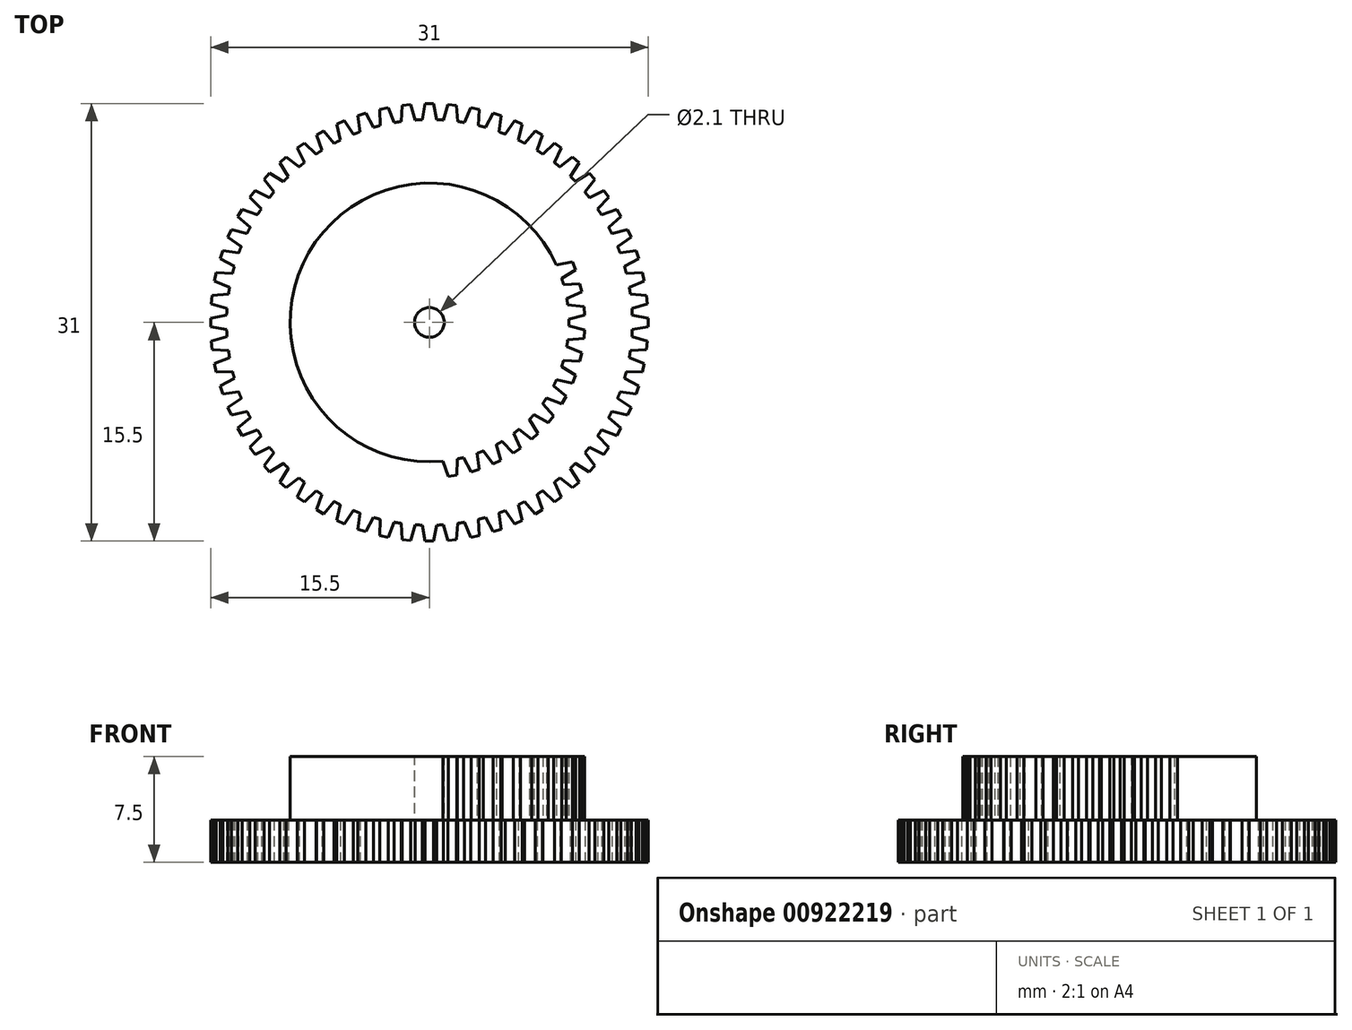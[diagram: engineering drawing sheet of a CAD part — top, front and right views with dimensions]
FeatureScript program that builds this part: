
annotation { "Feature Type Name" : "Feature", "Feature Type Description" : "" }
export const myFeature = defineFeature(function(context is Context, id is Id, definition is map)
    precondition{}
    {
        {
            var Q0;
            Q0=qCreatedBy(makeId("Top.planeOp"),FACE);
            var sketch = newSketch(context, id + "F0", { "sketchPlane" : qUnion([Q0])});
            skCircle(sketch, "E0", {"center": v(0, 0) * mm, "radius": 15 * mm, "construction": true});
            skCircle(sketch, "E1", {"center": v(0, 0) * mm, "radius": 15.5 * mm, "construction": true});
            skCircle(sketch, "E2", {"center": v(0, 0) * mm, "radius": 14.38 * mm});
            skLineSegment(sketch, "E3", {"start": v(0, 14.38) * mm, "end": v(0.5, 14.38) * mm, "construction": true});
            skLineSegment(sketch, "E4", {"start": v(0, 14.38) * mm, "end": v(-0.5, 14.38) * mm, "construction": true});
            skLineSegment(sketch, "E5", {"start": v(-1.79, 7.07) * mm, "end": v(-0.5, 14.37) * mm, "construction": true});
            skLineSegment(sketch, "E6", {"start": v(1.79, 7.07) * mm, "end": v(0.3, 15.5) * mm, "construction": true});
            skLineSegment(sketch, "E7", {"start": v(-1.79, 7.08) * mm, "end": v(-0.3, 15.5) * mm});
            skLineSegment(sketch, "E8", {"start": v(0.3, 15.5) * mm, "end": v(-0.3, 15.5) * mm});
            skLineSegment(sketch, "E9", {"start": v(0.3, 15.5) * mm, "end": v(0.5, 14.37) * mm});
            skLineSegment(sketch, "E10.1.0", {"start": v(-2.52, 6.85) * mm, "end": v(-1.92, 15.38) * mm});
            skLineSegment(sketch, "E10.1.1", {"start": v(-1.32, 15.44) * mm, "end": v(-1.92, 15.38) * mm});
            skLineSegment(sketch, "E10.1.2", {"start": v(-1.32, 15.44) * mm, "end": v(-1, 14.34) * mm});
            skLineSegment(sketch, "E10.2.0", {"start": v(-3.22, 6.55) * mm, "end": v(-3.52, 15.1) * mm});
            skLineSegment(sketch, "E10.2.1", {"start": v(-2.93, 15.22) * mm, "end": v(-3.52, 15.1) * mm});
            skLineSegment(sketch, "E10.2.2", {"start": v(-2.93, 15.22) * mm, "end": v(-2.5, 14.16) * mm});
            skLineSegment(sketch, "E11.1.3.0", {"start": v(-3.89, 6.18) * mm, "end": v(-5.08, 14.65) * mm});
            skLineSegment(sketch, "E11.3.3.0", {"start": v(-4.5, 14.83) * mm, "end": v(-5.08, 14.65) * mm});
            skLineSegment(sketch, "E11.6.3.0", {"start": v(-4.5, 14.83) * mm, "end": v(-3.96, 13.82) * mm});
            skLineSegment(sketch, "E11.1.4.0", {"start": v(-4.51, 5.74) * mm, "end": v(-6.58, 14.03) * mm});
            skLineSegment(sketch, "E11.3.4.0", {"start": v(-6.03, 14.28) * mm, "end": v(-6.58, 14.03) * mm});
            skLineSegment(sketch, "E11.6.4.0", {"start": v(-6.03, 14.28) * mm, "end": v(-5.39, 13.33) * mm});
            skLineSegment(sketch, "E11.1.5.0", {"start": v(-5.09, 5.24) * mm, "end": v(-8.01, 13.27) * mm});
            skLineSegment(sketch, "E11.3.5.0", {"start": v(-7.49, 13.57) * mm, "end": v(-8.01, 13.27) * mm});
            skLineSegment(sketch, "E11.6.5.0", {"start": v(-7.49, 13.57) * mm, "end": v(-6.75, 12.7) * mm});
            skLineSegment(sketch, "E11.1.6.0", {"start": v(-5.6, 4.68) * mm, "end": v(-9.35, 12.36) * mm});
            skLineSegment(sketch, "E11.3.6.0", {"start": v(-8.86, 12.71) * mm, "end": v(-9.35, 12.36) * mm});
            skLineSegment(sketch, "E11.6.6.0", {"start": v(-8.86, 12.71) * mm, "end": v(-8.04, 11.92) * mm});
            skLineSegment(sketch, "E11.1.7.0", {"start": v(-6.06, 4.07) * mm, "end": v(-10.6, 11.31) * mm});
            skLineSegment(sketch, "E11.3.7.0", {"start": v(-10.15, 11.72) * mm, "end": v(-10.6, 11.31) * mm});
            skLineSegment(sketch, "E11.6.7.0", {"start": v(-10.15, 11.72) * mm, "end": v(-9.24, 11.01) * mm});
            skLineSegment(sketch, "E11.1.8.0", {"start": v(-6.46, 3.4) * mm, "end": v(-11.72, 10.15) * mm});
            skLineSegment(sketch, "E11.3.8.0", {"start": v(-11.31, 10.6) * mm, "end": v(-11.72, 10.15) * mm});
            skLineSegment(sketch, "E11.6.8.0", {"start": v(-11.31, 10.6) * mm, "end": v(-10.34, 9.99) * mm});
            skLineSegment(sketch, "E11.1.9.0", {"start": v(-6.78, 2.72) * mm, "end": v(-12.71, 8.86) * mm});
            skLineSegment(sketch, "E11.3.9.0", {"start": v(-12.36, 9.35) * mm, "end": v(-12.71, 8.86) * mm});
            skLineSegment(sketch, "E11.6.9.0", {"start": v(-12.36, 9.35) * mm, "end": v(-11.33, 8.85) * mm});
            skLineSegment(sketch, "E11.1.10.0", {"start": v(-7.02, 2) * mm, "end": v(-13.57, 7.49) * mm});
            skLineSegment(sketch, "E11.3.10.0", {"start": v(-13.27, 8.01) * mm, "end": v(-13.57, 7.49) * mm});
            skLineSegment(sketch, "E11.6.10.0", {"start": v(-13.27, 8.01) * mm, "end": v(-12.2, 7.62) * mm});
            skLineSegment(sketch, "E11.1.11.0", {"start": v(-7.2, 1.25) * mm, "end": v(-14.28, 6.03) * mm});
            skLineSegment(sketch, "E11.3.11.0", {"start": v(-14.03, 6.58) * mm, "end": v(-14.28, 6.03) * mm});
            skLineSegment(sketch, "E11.6.11.0", {"start": v(-14.03, 6.58) * mm, "end": v(-12.92, 6.3) * mm});
            skLineSegment(sketch, "E11.1.12.0", {"start": v(-7.28, 0.49) * mm, "end": v(-14.83, 4.5) * mm});
            skLineSegment(sketch, "E11.3.12.0", {"start": v(-14.65, 5.08) * mm, "end": v(-14.83, 4.5) * mm});
            skLineSegment(sketch, "E11.6.12.0", {"start": v(-14.65, 5.08) * mm, "end": v(-13.5, 4.92) * mm});
            skLineSegment(sketch, "E11.1.13.0", {"start": v(-7.3, -0.28) * mm, "end": v(-15.22, 2.93) * mm});
            skLineSegment(sketch, "E11.3.13.0", {"start": v(-15.1, 3.52) * mm, "end": v(-15.22, 2.93) * mm});
            skLineSegment(sketch, "E11.6.13.0", {"start": v(-15.1, 3.52) * mm, "end": v(-13.95, 3.48) * mm});
            skLineSegment(sketch, "E11.1.14.0", {"start": v(-7.23, -1.04) * mm, "end": v(-15.44, 1.32) * mm});
            skLineSegment(sketch, "E11.3.14.0", {"start": v(-15.38, 1.92) * mm, "end": v(-15.44, 1.32) * mm});
            skLineSegment(sketch, "E11.6.14.0", {"start": v(-15.38, 1.92) * mm, "end": v(-14.24, 2) * mm});
            skLineSegment(sketch, "E11.1.15.0", {"start": v(-7.08, -1.79) * mm, "end": v(-15.5, -0.3) * mm});
            skLineSegment(sketch, "E11.3.15.0", {"start": v(-15.5, 0.3) * mm, "end": v(-15.5, -0.3) * mm});
            skLineSegment(sketch, "E11.6.15.0", {"start": v(-15.5, 0.3) * mm, "end": v(-14.37, 0.5) * mm});
            skLineSegment(sketch, "E11.1.16.0", {"start": v(-6.85, -2.52) * mm, "end": v(-15.38, -1.92) * mm});
            skLineSegment(sketch, "E11.3.16.0", {"start": v(-15.44, -1.32) * mm, "end": v(-15.38, -1.92) * mm});
            skLineSegment(sketch, "E11.6.16.0", {"start": v(-15.44, -1.32) * mm, "end": v(-14.34, -1) * mm});
            skLineSegment(sketch, "E11.1.17.0", {"start": v(-6.55, -3.22) * mm, "end": v(-15.1, -3.52) * mm});
            skLineSegment(sketch, "E11.3.17.0", {"start": v(-15.22, -2.93) * mm, "end": v(-15.1, -3.52) * mm});
            skLineSegment(sketch, "E11.6.17.0", {"start": v(-15.22, -2.93) * mm, "end": v(-14.16, -2.5) * mm});
            skLineSegment(sketch, "E11.1.18.0", {"start": v(-6.18, -3.89) * mm, "end": v(-14.65, -5.08) * mm});
            skLineSegment(sketch, "E11.3.18.0", {"start": v(-14.83, -4.5) * mm, "end": v(-14.65, -5.08) * mm});
            skLineSegment(sketch, "E11.6.18.0", {"start": v(-14.83, -4.5) * mm, "end": v(-13.82, -3.96) * mm});
            skLineSegment(sketch, "E11.1.19.0", {"start": v(-5.74, -4.51) * mm, "end": v(-14.03, -6.58) * mm});
            skLineSegment(sketch, "E11.3.19.0", {"start": v(-14.28, -6.03) * mm, "end": v(-14.03, -6.58) * mm});
            skLineSegment(sketch, "E11.6.19.0", {"start": v(-14.28, -6.03) * mm, "end": v(-13.33, -5.39) * mm});
            skLineSegment(sketch, "E11.1.20.0", {"start": v(-5.24, -5.09) * mm, "end": v(-13.27, -8.01) * mm});
            skLineSegment(sketch, "E11.3.20.0", {"start": v(-13.57, -7.49) * mm, "end": v(-13.27, -8.01) * mm});
            skLineSegment(sketch, "E11.6.20.0", {"start": v(-13.57, -7.49) * mm, "end": v(-12.7, -6.75) * mm});
            skLineSegment(sketch, "E11.1.21.0", {"start": v(-4.68, -5.6) * mm, "end": v(-12.36, -9.35) * mm});
            skLineSegment(sketch, "E11.3.21.0", {"start": v(-12.71, -8.86) * mm, "end": v(-12.36, -9.35) * mm});
            skLineSegment(sketch, "E11.6.21.0", {"start": v(-12.71, -8.86) * mm, "end": v(-11.92, -8.04) * mm});
            skLineSegment(sketch, "E11.1.22.0", {"start": v(-4.07, -6.06) * mm, "end": v(-11.31, -10.6) * mm});
            skLineSegment(sketch, "E11.3.22.0", {"start": v(-11.72, -10.15) * mm, "end": v(-11.31, -10.6) * mm});
            skLineSegment(sketch, "E11.6.22.0", {"start": v(-11.72, -10.15) * mm, "end": v(-11.01, -9.24) * mm});
            skLineSegment(sketch, "E11.1.23.0", {"start": v(-3.4, -6.46) * mm, "end": v(-10.15, -11.72) * mm});
            skLineSegment(sketch, "E11.3.23.0", {"start": v(-10.6, -11.31) * mm, "end": v(-10.15, -11.72) * mm});
            skLineSegment(sketch, "E11.6.23.0", {"start": v(-10.6, -11.31) * mm, "end": v(-9.99, -10.34) * mm});
            skLineSegment(sketch, "E11.1.24.0", {"start": v(-2.72, -6.78) * mm, "end": v(-8.86, -12.71) * mm});
            skLineSegment(sketch, "E11.3.24.0", {"start": v(-9.35, -12.36) * mm, "end": v(-8.86, -12.71) * mm});
            skLineSegment(sketch, "E11.6.24.0", {"start": v(-9.35, -12.36) * mm, "end": v(-8.85, -11.33) * mm});
            skLineSegment(sketch, "E11.1.25.0", {"start": v(-2, -7.02) * mm, "end": v(-7.49, -13.57) * mm});
            skLineSegment(sketch, "E11.3.25.0", {"start": v(-8.01, -13.27) * mm, "end": v(-7.49, -13.57) * mm});
            skLineSegment(sketch, "E11.6.25.0", {"start": v(-8.01, -13.27) * mm, "end": v(-7.62, -12.2) * mm});
            skLineSegment(sketch, "E11.1.26.0", {"start": v(-1.25, -7.2) * mm, "end": v(-6.03, -14.28) * mm});
            skLineSegment(sketch, "E11.3.26.0", {"start": v(-6.58, -14.03) * mm, "end": v(-6.03, -14.28) * mm});
            skLineSegment(sketch, "E11.6.26.0", {"start": v(-6.58, -14.03) * mm, "end": v(-6.3, -12.92) * mm});
            skLineSegment(sketch, "E11.1.27.0", {"start": v(-0.49, -7.28) * mm, "end": v(-4.5, -14.83) * mm});
            skLineSegment(sketch, "E11.3.27.0", {"start": v(-5.08, -14.65) * mm, "end": v(-4.5, -14.83) * mm});
            skLineSegment(sketch, "E11.6.27.0", {"start": v(-5.08, -14.65) * mm, "end": v(-4.92, -13.5) * mm});
            skLineSegment(sketch, "E11.1.28.0", {"start": v(0.28, -7.3) * mm, "end": v(-2.93, -15.22) * mm});
            skLineSegment(sketch, "E11.3.28.0", {"start": v(-3.52, -15.1) * mm, "end": v(-2.93, -15.22) * mm});
            skLineSegment(sketch, "E11.6.28.0", {"start": v(-3.52, -15.1) * mm, "end": v(-3.48, -13.95) * mm});
            skLineSegment(sketch, "E11.1.29.0", {"start": v(1.04, -7.23) * mm, "end": v(-1.32, -15.44) * mm});
            skLineSegment(sketch, "E11.3.29.0", {"start": v(-1.92, -15.38) * mm, "end": v(-1.32, -15.44) * mm});
            skLineSegment(sketch, "E11.6.29.0", {"start": v(-1.92, -15.38) * mm, "end": v(-2, -14.24) * mm});
            skLineSegment(sketch, "E12.1.30.0", {"start": v(1.79, -7.08) * mm, "end": v(0.3, -15.5) * mm});
            skLineSegment(sketch, "E12.3.30.0", {"start": v(-0.3, -15.5) * mm, "end": v(0.3, -15.5) * mm});
            skLineSegment(sketch, "E12.6.30.0", {"start": v(-0.3, -15.5) * mm, "end": v(-0.5, -14.37) * mm});
            skLineSegment(sketch, "E12.1.31.0", {"start": v(2.52, -6.85) * mm, "end": v(1.92, -15.38) * mm});
            skLineSegment(sketch, "E12.3.31.0", {"start": v(1.32, -15.44) * mm, "end": v(1.92, -15.38) * mm});
            skLineSegment(sketch, "E12.6.31.0", {"start": v(1.32, -15.44) * mm, "end": v(1, -14.34) * mm});
            skLineSegment(sketch, "E12.1.32.0", {"start": v(3.22, -6.55) * mm, "end": v(3.52, -15.1) * mm});
            skLineSegment(sketch, "E12.3.32.0", {"start": v(2.93, -15.22) * mm, "end": v(3.52, -15.1) * mm});
            skLineSegment(sketch, "E12.6.32.0", {"start": v(2.93, -15.22) * mm, "end": v(2.5, -14.16) * mm});
            skLineSegment(sketch, "E12.1.33.0", {"start": v(3.89, -6.18) * mm, "end": v(5.08, -14.65) * mm});
            skLineSegment(sketch, "E12.3.33.0", {"start": v(4.5, -14.83) * mm, "end": v(5.08, -14.65) * mm});
            skLineSegment(sketch, "E12.6.33.0", {"start": v(4.5, -14.83) * mm, "end": v(3.96, -13.82) * mm});
            skLineSegment(sketch, "E12.1.34.0", {"start": v(4.51, -5.74) * mm, "end": v(6.58, -14.03) * mm});
            skLineSegment(sketch, "E12.3.34.0", {"start": v(6.03, -14.28) * mm, "end": v(6.58, -14.03) * mm});
            skLineSegment(sketch, "E12.6.34.0", {"start": v(6.03, -14.28) * mm, "end": v(5.39, -13.33) * mm});
            skLineSegment(sketch, "E12.1.35.0", {"start": v(5.09, -5.24) * mm, "end": v(8.01, -13.27) * mm});
            skLineSegment(sketch, "E12.3.35.0", {"start": v(7.49, -13.57) * mm, "end": v(8.01, -13.27) * mm});
            skLineSegment(sketch, "E12.6.35.0", {"start": v(7.49, -13.57) * mm, "end": v(6.75, -12.7) * mm});
            skLineSegment(sketch, "E12.1.36.0", {"start": v(5.6, -4.68) * mm, "end": v(9.35, -12.36) * mm});
            skLineSegment(sketch, "E12.3.36.0", {"start": v(8.86, -12.71) * mm, "end": v(9.35, -12.36) * mm});
            skLineSegment(sketch, "E12.6.36.0", {"start": v(8.86, -12.71) * mm, "end": v(8.04, -11.92) * mm});
            skLineSegment(sketch, "E12.1.37.0", {"start": v(6.06, -4.07) * mm, "end": v(10.6, -11.31) * mm});
            skLineSegment(sketch, "E12.3.37.0", {"start": v(10.15, -11.72) * mm, "end": v(10.6, -11.31) * mm});
            skLineSegment(sketch, "E12.6.37.0", {"start": v(10.15, -11.72) * mm, "end": v(9.24, -11.01) * mm});
            skLineSegment(sketch, "E12.1.38.0", {"start": v(6.46, -3.4) * mm, "end": v(11.72, -10.15) * mm});
            skLineSegment(sketch, "E12.3.38.0", {"start": v(11.31, -10.6) * mm, "end": v(11.72, -10.15) * mm});
            skLineSegment(sketch, "E12.6.38.0", {"start": v(11.31, -10.6) * mm, "end": v(10.34, -9.99) * mm});
            skLineSegment(sketch, "E12.1.39.0", {"start": v(6.78, -2.72) * mm, "end": v(12.71, -8.86) * mm});
            skLineSegment(sketch, "E12.3.39.0", {"start": v(12.36, -9.35) * mm, "end": v(12.71, -8.86) * mm});
            skLineSegment(sketch, "E12.6.39.0", {"start": v(12.36, -9.35) * mm, "end": v(11.33, -8.85) * mm});
            skLineSegment(sketch, "E12.1.40.0", {"start": v(7.02, -2) * mm, "end": v(13.57, -7.49) * mm});
            skLineSegment(sketch, "E12.3.40.0", {"start": v(13.27, -8.01) * mm, "end": v(13.57, -7.49) * mm});
            skLineSegment(sketch, "E12.6.40.0", {"start": v(13.27, -8.01) * mm, "end": v(12.2, -7.62) * mm});
            skLineSegment(sketch, "E12.1.41.0", {"start": v(7.2, -1.25) * mm, "end": v(14.28, -6.03) * mm});
            skLineSegment(sketch, "E12.3.41.0", {"start": v(14.03, -6.58) * mm, "end": v(14.28, -6.03) * mm});
            skLineSegment(sketch, "E12.6.41.0", {"start": v(14.03, -6.58) * mm, "end": v(12.92, -6.3) * mm});
            skLineSegment(sketch, "E13.1.42.0", {"start": v(7.28, -0.49) * mm, "end": v(14.83, -4.5) * mm});
            skLineSegment(sketch, "E13.3.42.0", {"start": v(14.65, -5.08) * mm, "end": v(14.83, -4.5) * mm});
            skLineSegment(sketch, "E13.6.42.0", {"start": v(14.65, -5.08) * mm, "end": v(13.5, -4.92) * mm});
            skLineSegment(sketch, "E13.1.43.0", {"start": v(7.3, 0.28) * mm, "end": v(15.22, -2.93) * mm});
            skLineSegment(sketch, "E13.3.43.0", {"start": v(15.1, -3.52) * mm, "end": v(15.22, -2.93) * mm});
            skLineSegment(sketch, "E13.6.43.0", {"start": v(15.1, -3.52) * mm, "end": v(13.95, -3.48) * mm});
            skLineSegment(sketch, "E13.1.44.0", {"start": v(7.23, 1.04) * mm, "end": v(15.44, -1.32) * mm});
            skLineSegment(sketch, "E13.3.44.0", {"start": v(15.38, -1.92) * mm, "end": v(15.44, -1.32) * mm});
            skLineSegment(sketch, "E13.6.44.0", {"start": v(15.38, -1.92) * mm, "end": v(14.24, -2) * mm});
            skLineSegment(sketch, "E13.1.45.0", {"start": v(7.08, 1.79) * mm, "end": v(15.5, 0.3) * mm});
            skLineSegment(sketch, "E13.3.45.0", {"start": v(15.5, -0.3) * mm, "end": v(15.5, 0.3) * mm});
            skLineSegment(sketch, "E13.6.45.0", {"start": v(15.5, -0.3) * mm, "end": v(14.37, -0.5) * mm});
            skLineSegment(sketch, "E13.1.46.0", {"start": v(6.85, 2.52) * mm, "end": v(15.38, 1.92) * mm});
            skLineSegment(sketch, "E13.3.46.0", {"start": v(15.44, 1.32) * mm, "end": v(15.38, 1.92) * mm});
            skLineSegment(sketch, "E13.6.46.0", {"start": v(15.44, 1.32) * mm, "end": v(14.34, 1) * mm});
            skLineSegment(sketch, "E13.1.47.0", {"start": v(6.55, 3.22) * mm, "end": v(15.1, 3.52) * mm});
            skLineSegment(sketch, "E13.3.47.0", {"start": v(15.22, 2.93) * mm, "end": v(15.1, 3.52) * mm});
            skLineSegment(sketch, "E13.6.47.0", {"start": v(15.22, 2.93) * mm, "end": v(14.16, 2.5) * mm});
            skLineSegment(sketch, "E14.1.48.0", {"start": v(6.18, 3.89) * mm, "end": v(14.65, 5.08) * mm});
            skLineSegment(sketch, "E14.3.48.0", {"start": v(14.83, 4.5) * mm, "end": v(14.65, 5.08) * mm});
            skLineSegment(sketch, "E14.6.48.0", {"start": v(14.83, 4.5) * mm, "end": v(13.82, 3.96) * mm});
            skLineSegment(sketch, "E14.1.49.0", {"start": v(5.74, 4.51) * mm, "end": v(14.03, 6.58) * mm});
            skLineSegment(sketch, "E14.3.49.0", {"start": v(14.28, 6.03) * mm, "end": v(14.03, 6.58) * mm});
            skLineSegment(sketch, "E14.6.49.0", {"start": v(14.28, 6.03) * mm, "end": v(13.33, 5.39) * mm});
            skLineSegment(sketch, "E14.1.50.0", {"start": v(5.24, 5.09) * mm, "end": v(13.27, 8.01) * mm});
            skLineSegment(sketch, "E14.3.50.0", {"start": v(13.57, 7.49) * mm, "end": v(13.27, 8.01) * mm});
            skLineSegment(sketch, "E14.6.50.0", {"start": v(13.57, 7.49) * mm, "end": v(12.7, 6.75) * mm});
            skLineSegment(sketch, "E14.1.51.0", {"start": v(4.68, 5.6) * mm, "end": v(12.36, 9.35) * mm});
            skLineSegment(sketch, "E14.3.51.0", {"start": v(12.71, 8.86) * mm, "end": v(12.36, 9.35) * mm});
            skLineSegment(sketch, "E14.6.51.0", {"start": v(12.71, 8.86) * mm, "end": v(11.92, 8.04) * mm});
            skLineSegment(sketch, "E14.1.52.0", {"start": v(4.07, 6.06) * mm, "end": v(11.31, 10.6) * mm});
            skLineSegment(sketch, "E14.3.52.0", {"start": v(11.72, 10.15) * mm, "end": v(11.31, 10.6) * mm});
            skLineSegment(sketch, "E14.6.52.0", {"start": v(11.72, 10.15) * mm, "end": v(11.01, 9.24) * mm});
            skLineSegment(sketch, "E14.1.53.0", {"start": v(3.4, 6.46) * mm, "end": v(10.15, 11.72) * mm});
            skLineSegment(sketch, "E14.3.53.0", {"start": v(10.6, 11.31) * mm, "end": v(10.15, 11.72) * mm});
            skLineSegment(sketch, "E14.6.53.0", {"start": v(10.6, 11.31) * mm, "end": v(9.99, 10.34) * mm});
            skLineSegment(sketch, "E15.1.54.0", {"start": v(2.72, 6.78) * mm, "end": v(8.86, 12.71) * mm});
            skLineSegment(sketch, "E15.3.54.0", {"start": v(9.35, 12.36) * mm, "end": v(8.86, 12.71) * mm});
            skLineSegment(sketch, "E15.6.54.0", {"start": v(9.35, 12.36) * mm, "end": v(8.85, 11.33) * mm});
            skLineSegment(sketch, "E15.1.55.0", {"start": v(2, 7.02) * mm, "end": v(7.49, 13.57) * mm});
            skLineSegment(sketch, "E15.3.55.0", {"start": v(8.01, 13.27) * mm, "end": v(7.49, 13.57) * mm});
            skLineSegment(sketch, "E15.6.55.0", {"start": v(8.01, 13.27) * mm, "end": v(7.62, 12.2) * mm});
            skLineSegment(sketch, "E15.1.56.0", {"start": v(1.25, 7.2) * mm, "end": v(6.03, 14.28) * mm});
            skLineSegment(sketch, "E15.3.56.0", {"start": v(6.58, 14.03) * mm, "end": v(6.03, 14.28) * mm});
            skLineSegment(sketch, "E15.6.56.0", {"start": v(6.58, 14.03) * mm, "end": v(6.3, 12.92) * mm});
            skLineSegment(sketch, "E15.1.57.0", {"start": v(0.49, 7.28) * mm, "end": v(4.5, 14.83) * mm});
            skLineSegment(sketch, "E15.3.57.0", {"start": v(5.08, 14.65) * mm, "end": v(4.5, 14.83) * mm});
            skLineSegment(sketch, "E15.6.57.0", {"start": v(5.08, 14.65) * mm, "end": v(4.92, 13.5) * mm});
            skLineSegment(sketch, "E15.1.58.0", {"start": v(-0.28, 7.3) * mm, "end": v(2.93, 15.22) * mm});
            skLineSegment(sketch, "E15.3.58.0", {"start": v(3.52, 15.1) * mm, "end": v(2.93, 15.22) * mm});
            skLineSegment(sketch, "E15.6.58.0", {"start": v(3.52, 15.1) * mm, "end": v(3.48, 13.95) * mm});
            skLineSegment(sketch, "E15.1.59.0", {"start": v(-1.04, 7.23) * mm, "end": v(1.32, 15.44) * mm});
            skLineSegment(sketch, "E15.3.59.0", {"start": v(1.92, 15.38) * mm, "end": v(1.32, 15.44) * mm});
            skLineSegment(sketch, "E15.6.59.0", {"start": v(1.92, 15.38) * mm, "end": v(2, 14.24) * mm});
            skSolve(sketch);
        }
        {
            var Q0;
            Q0=qSketchRegion(id+"F0",true);
            extrude(context, id + "F1", {"entities" : qUnion([Q0]), "depth" : 3 * mm, "offsetDistance" : 25 * mm});
        }
        {
            var Q0;
            Q0=makeQuery(id+"F1.opExtrude","CAP_FACE",FACE,{"disambiguationData":[OSD([sQuery(id+"F0.wireOp",EDGE,"E2"),sQuery(id+"F0.wireOp",EDGE,"E7"),sQuery(id+"F0.wireOp",EDGE,"E8"),sQuery(id+"F0.wireOp",EDGE,"E9"),sQuery(id+"F0.wireOp",EDGE,"E10.1.0"),sQuery(id+"F0.wireOp",EDGE,"E10.1.1"),sQuery(id+"F0.wireOp",EDGE,"E10.1.2"),sQuery(id+"F0.wireOp",EDGE,"E10.2.0"),sQuery(id+"F0.wireOp",EDGE,"E10.2.1"),sQuery(id+"F0.wireOp",EDGE,"E10.2.2"),sQuery(id+"F0.wireOp",EDGE,"E11.1.3.0"),sQuery(id+"F0.wireOp",EDGE,"E11.3.3.0"),sQuery(id+"F0.wireOp",EDGE,"E11.6.3.0"),sQuery(id+"F0.wireOp",EDGE,"E11.1.4.0"),sQuery(id+"F0.wireOp",EDGE,"E11.3.4.0"),sQuery(id+"F0.wireOp",EDGE,"E11.6.4.0"),sQuery(id+"F0.wireOp",EDGE,"E11.1.5.0"),sQuery(id+"F0.wireOp",EDGE,"E11.3.5.0"),sQuery(id+"F0.wireOp",EDGE,"E11.6.5.0"),sQuery(id+"F0.wireOp",EDGE,"E11.1.6.0"),sQuery(id+"F0.wireOp",EDGE,"E11.3.6.0"),sQuery(id+"F0.wireOp",EDGE,"E11.6.6.0"),sQuery(id+"F0.wireOp",EDGE,"E11.1.7.0"),sQuery(id+"F0.wireOp",EDGE,"E11.3.7.0"),sQuery(id+"F0.wireOp",EDGE,"E11.6.7.0"),sQuery(id+"F0.wireOp",EDGE,"E11.1.8.0"),sQuery(id+"F0.wireOp",EDGE,"E11.3.8.0"),sQuery(id+"F0.wireOp",EDGE,"E11.6.8.0"),sQuery(id+"F0.wireOp",EDGE,"E11.1.9.0"),sQuery(id+"F0.wireOp",EDGE,"E11.3.9.0"),sQuery(id+"F0.wireOp",EDGE,"E11.6.9.0"),sQuery(id+"F0.wireOp",EDGE,"E11.1.10.0"),sQuery(id+"F0.wireOp",EDGE,"E11.3.10.0"),sQuery(id+"F0.wireOp",EDGE,"E11.6.10.0"),sQuery(id+"F0.wireOp",EDGE,"E11.1.11.0"),sQuery(id+"F0.wireOp",EDGE,"E11.3.11.0"),sQuery(id+"F0.wireOp",EDGE,"E11.6.11.0"),sQuery(id+"F0.wireOp",EDGE,"E11.1.12.0"),sQuery(id+"F0.wireOp",EDGE,"E11.3.12.0"),sQuery(id+"F0.wireOp",EDGE,"E11.6.12.0"),sQuery(id+"F0.wireOp",EDGE,"E11.1.13.0"),sQuery(id+"F0.wireOp",EDGE,"E11.3.13.0"),sQuery(id+"F0.wireOp",EDGE,"E11.6.13.0"),sQuery(id+"F0.wireOp",EDGE,"E11.1.14.0"),sQuery(id+"F0.wireOp",EDGE,"E11.3.14.0"),sQuery(id+"F0.wireOp",EDGE,"E11.6.14.0"),sQuery(id+"F0.wireOp",EDGE,"E11.1.15.0"),sQuery(id+"F0.wireOp",EDGE,"E11.3.15.0"),sQuery(id+"F0.wireOp",EDGE,"E11.6.15.0"),sQuery(id+"F0.wireOp",EDGE,"E11.1.16.0"),sQuery(id+"F0.wireOp",EDGE,"E11.3.16.0"),sQuery(id+"F0.wireOp",EDGE,"E11.6.16.0"),sQuery(id+"F0.wireOp",EDGE,"E11.1.17.0"),sQuery(id+"F0.wireOp",EDGE,"E11.3.17.0"),sQuery(id+"F0.wireOp",EDGE,"E11.6.17.0"),sQuery(id+"F0.wireOp",EDGE,"E11.1.18.0"),sQuery(id+"F0.wireOp",EDGE,"E11.3.18.0"),sQuery(id+"F0.wireOp",EDGE,"E11.6.18.0"),sQuery(id+"F0.wireOp",EDGE,"E11.1.19.0"),sQuery(id+"F0.wireOp",EDGE,"E11.3.19.0"),sQuery(id+"F0.wireOp",EDGE,"E11.6.19.0"),sQuery(id+"F0.wireOp",EDGE,"E11.1.20.0"),sQuery(id+"F0.wireOp",EDGE,"E11.3.20.0"),sQuery(id+"F0.wireOp",EDGE,"E11.6.20.0"),sQuery(id+"F0.wireOp",EDGE,"E11.1.21.0"),sQuery(id+"F0.wireOp",EDGE,"E11.3.21.0"),sQuery(id+"F0.wireOp",EDGE,"E11.6.21.0"),sQuery(id+"F0.wireOp",EDGE,"E11.1.22.0"),sQuery(id+"F0.wireOp",EDGE,"E11.3.22.0"),sQuery(id+"F0.wireOp",EDGE,"E11.6.22.0"),sQuery(id+"F0.wireOp",EDGE,"E11.1.23.0"),sQuery(id+"F0.wireOp",EDGE,"E11.3.23.0"),sQuery(id+"F0.wireOp",EDGE,"E11.6.23.0"),sQuery(id+"F0.wireOp",EDGE,"E11.1.24.0"),sQuery(id+"F0.wireOp",EDGE,"E11.3.24.0"),sQuery(id+"F0.wireOp",EDGE,"E11.6.24.0"),sQuery(id+"F0.wireOp",EDGE,"E11.1.25.0"),sQuery(id+"F0.wireOp",EDGE,"E11.3.25.0"),sQuery(id+"F0.wireOp",EDGE,"E11.6.25.0"),sQuery(id+"F0.wireOp",EDGE,"E11.1.26.0"),sQuery(id+"F0.wireOp",EDGE,"E11.3.26.0"),sQuery(id+"F0.wireOp",EDGE,"E11.6.26.0"),sQuery(id+"F0.wireOp",EDGE,"E11.1.27.0"),sQuery(id+"F0.wireOp",EDGE,"E11.3.27.0"),sQuery(id+"F0.wireOp",EDGE,"E11.6.27.0"),sQuery(id+"F0.wireOp",EDGE,"E11.1.28.0"),sQuery(id+"F0.wireOp",EDGE,"E11.3.28.0"),sQuery(id+"F0.wireOp",EDGE,"E11.6.28.0"),sQuery(id+"F0.wireOp",EDGE,"E11.1.29.0"),sQuery(id+"F0.wireOp",EDGE,"E11.3.29.0"),sQuery(id+"F0.wireOp",EDGE,"E11.6.29.0")])],"isStart":false});
            var sketch = newSketch(context, id + "F2", { "sketchPlane" : qUnion([Q0])});
            skCircle(sketch, "E16", {"center": v(0, 0) * mm, "radius": 10.5 * mm, "construction": true});
            skCircle(sketch, "E17", {"center": v(0, 0) * mm, "radius": 11 * mm, "construction": true});
            skCircle(sketch, "E18", {"center": v(0, 0) * mm, "radius": 9.88 * mm});
            skLineSegment(sketch, "E19", {"start": v(0, 9.88) * mm, "end": v(0.5, 9.88) * mm, "construction": true});
            skLineSegment(sketch, "E20", {"start": v(0, 9.88) * mm, "end": v(-0.5, 9.88) * mm, "construction": true});
            skLineSegment(sketch, "E21", {"start": v(-0.5, 9.86) * mm, "end": v(-0.3, 11) * mm, "construction": true});
            skLineSegment(sketch, "E22", {"start": v(0.5, 9.86) * mm, "end": v(0.3, 11) * mm, "construction": true});
            skLineSegment(sketch, "E23", {"start": v(-0.5, 9.86) * mm, "end": v(-0.3, 11) * mm});
            skLineSegment(sketch, "E24", {"start": v(0.3, 11) * mm, "end": v(-0.3, 11) * mm});
            skLineSegment(sketch, "E25", {"start": v(0.3, 11) * mm, "end": v(0.5, 9.86) * mm});
            skLineSegment(sketch, "E26.1.0", {"start": v(-1.97, 9.68) * mm, "end": v(-1.94, 10.83) * mm});
            skLineSegment(sketch, "E26.1.1", {"start": v(-1.34, 10.92) * mm, "end": v(-1.94, 10.83) * mm});
            skLineSegment(sketch, "E26.1.2", {"start": v(-1.34, 10.92) * mm, "end": v(-0.97, 9.83) * mm});
            skLineSegment(sketch, "E26.2.0", {"start": v(-3.39, 9.28) * mm, "end": v(-3.53, 10.42) * mm});
            skLineSegment(sketch, "E26.2.1", {"start": v(-2.95, 10.6) * mm, "end": v(-3.53, 10.42) * mm});
            skLineSegment(sketch, "E26.2.2", {"start": v(-2.95, 10.6) * mm, "end": v(-2.43, 9.57) * mm});
            skLineSegment(sketch, "E27.1.3.0", {"start": v(-4.73, 8.67) * mm, "end": v(-5.04, 9.78) * mm});
            skLineSegment(sketch, "E27.3.3.0", {"start": v(-4.5, 10.04) * mm, "end": v(-5.04, 9.78) * mm});
            skLineSegment(sketch, "E27.6.3.0", {"start": v(-4.5, 10.04) * mm, "end": v(-3.83, 9.1) * mm});
            skLineSegment(sketch, "E27.1.4.0", {"start": v(-5.97, 7.87) * mm, "end": v(-6.44, 8.91) * mm});
            skLineSegment(sketch, "E27.3.4.0", {"start": v(-5.94, 9.26) * mm, "end": v(-6.44, 8.91) * mm});
            skLineSegment(sketch, "E27.6.4.0", {"start": v(-5.94, 9.26) * mm, "end": v(-5.14, 8.43) * mm});
            skLineSegment(sketch, "E27.1.5.0", {"start": v(-7.08, 6.89) * mm, "end": v(-7.7, 7.85) * mm});
            skLineSegment(sketch, "E27.3.5.0", {"start": v(-7.26, 8.27) * mm, "end": v(-7.7, 7.85) * mm});
            skLineSegment(sketch, "E27.6.5.0", {"start": v(-7.26, 8.27) * mm, "end": v(-6.34, 7.57) * mm});
            skLineSegment(sketch, "E27.1.6.0", {"start": v(-8.02, 5.76) * mm, "end": v(-8.79, 6.62) * mm});
            skLineSegment(sketch, "E27.3.6.0", {"start": v(-8.4, 7.1) * mm, "end": v(-8.79, 6.62) * mm});
            skLineSegment(sketch, "E27.6.6.0", {"start": v(-8.4, 7.1) * mm, "end": v(-7.4, 6.54) * mm});
            skLineSegment(sketch, "E27.1.7.0", {"start": v(-8.8, 4.5) * mm, "end": v(-9.67, 5.24) * mm});
            skLineSegment(sketch, "E27.3.7.0", {"start": v(-9.37, 5.76) * mm, "end": v(-9.67, 5.24) * mm});
            skLineSegment(sketch, "E27.6.7.0", {"start": v(-9.37, 5.76) * mm, "end": v(-8.29, 5.37) * mm});
            skLineSegment(sketch, "E27.1.8.0", {"start": v(-9.36, 3.14) * mm, "end": v(-10.35, 3.74) * mm});
            skLineSegment(sketch, "E27.3.8.0", {"start": v(-10.13, 4.3) * mm, "end": v(-10.35, 3.74) * mm});
            skLineSegment(sketch, "E27.6.8.0", {"start": v(-10.13, 4.3) * mm, "end": v(-9, 4.07) * mm});
            skLineSegment(sketch, "E27.1.9.0", {"start": v(-9.73, 1.7) * mm, "end": v(-10.79, 2.15) * mm});
            skLineSegment(sketch, "E27.3.9.0", {"start": v(-10.65, 2.74) * mm, "end": v(-10.79, 2.15) * mm});
            skLineSegment(sketch, "E27.6.9.0", {"start": v(-10.65, 2.74) * mm, "end": v(-9.5, 2.68) * mm});
            skLineSegment(sketch, "E28.1.10.0", {"start": v(-9.87, 0.24) * mm, "end": v(-10.99, 0.52) * mm});
            skLineSegment(sketch, "E28.3.10.0", {"start": v(-10.94, 1.12) * mm, "end": v(-10.99, 0.52) * mm});
            skLineSegment(sketch, "E28.6.10.0", {"start": v(-10.94, 1.12) * mm, "end": v(-9.8, 1.24) * mm});
            skLineSegment(sketch, "E28.1.11.0", {"start": v(-9.8, -1.24) * mm, "end": v(-10.94, -1.12) * mm});
            skLineSegment(sketch, "E28.3.11.0", {"start": v(-10.99, -0.52) * mm, "end": v(-10.94, -1.12) * mm});
            skLineSegment(sketch, "E28.6.11.0", {"start": v(-10.99, -0.52) * mm, "end": v(-9.87, -0.24) * mm});
            skLineSegment(sketch, "E28.1.12.0", {"start": v(-9.5, -2.68) * mm, "end": v(-10.65, -2.74) * mm});
            skLineSegment(sketch, "E28.3.12.0", {"start": v(-10.79, -2.15) * mm, "end": v(-10.65, -2.74) * mm});
            skLineSegment(sketch, "E28.6.12.0", {"start": v(-10.79, -2.15) * mm, "end": v(-9.73, -1.7) * mm});
            skLineSegment(sketch, "E28.1.13.0", {"start": v(-9, -4.07) * mm, "end": v(-10.13, -4.3) * mm});
            skLineSegment(sketch, "E28.3.13.0", {"start": v(-10.35, -3.74) * mm, "end": v(-10.13, -4.3) * mm});
            skLineSegment(sketch, "E28.6.13.0", {"start": v(-10.35, -3.74) * mm, "end": v(-9.36, -3.14) * mm});
            skLineSegment(sketch, "E28.1.14.0", {"start": v(-8.29, -5.37) * mm, "end": v(-9.37, -5.76) * mm});
            skLineSegment(sketch, "E28.3.14.0", {"start": v(-9.67, -5.24) * mm, "end": v(-9.37, -5.76) * mm});
            skLineSegment(sketch, "E28.6.14.0", {"start": v(-9.67, -5.24) * mm, "end": v(-8.8, -4.5) * mm});
            skLineSegment(sketch, "E28.1.15.0", {"start": v(-7.4, -6.54) * mm, "end": v(-8.4, -7.1) * mm});
            skLineSegment(sketch, "E28.3.15.0", {"start": v(-8.79, -6.62) * mm, "end": v(-8.4, -7.1) * mm});
            skLineSegment(sketch, "E28.6.15.0", {"start": v(-8.79, -6.62) * mm, "end": v(-8.02, -5.76) * mm});
            skLineSegment(sketch, "E28.1.16.0", {"start": v(-6.34, -7.57) * mm, "end": v(-7.26, -8.27) * mm});
            skLineSegment(sketch, "E28.3.16.0", {"start": v(-7.7, -7.85) * mm, "end": v(-7.26, -8.27) * mm});
            skLineSegment(sketch, "E28.6.16.0", {"start": v(-7.7, -7.85) * mm, "end": v(-7.08, -6.89) * mm});
            skLineSegment(sketch, "E28.1.17.0", {"start": v(-5.14, -8.43) * mm, "end": v(-5.94, -9.26) * mm});
            skLineSegment(sketch, "E28.3.17.0", {"start": v(-6.44, -8.91) * mm, "end": v(-5.94, -9.26) * mm});
            skLineSegment(sketch, "E28.6.17.0", {"start": v(-6.44, -8.91) * mm, "end": v(-5.97, -7.87) * mm});
            skLineSegment(sketch, "E28.1.18.0", {"start": v(-3.83, -9.1) * mm, "end": v(-4.5, -10.04) * mm});
            skLineSegment(sketch, "E28.3.18.0", {"start": v(-5.04, -9.78) * mm, "end": v(-4.5, -10.04) * mm});
            skLineSegment(sketch, "E28.6.18.0", {"start": v(-5.04, -9.78) * mm, "end": v(-4.73, -8.67) * mm});
            skLineSegment(sketch, "E28.1.19.0", {"start": v(-2.43, -9.57) * mm, "end": v(-2.95, -10.6) * mm});
            skLineSegment(sketch, "E28.3.19.0", {"start": v(-3.53, -10.42) * mm, "end": v(-2.95, -10.6) * mm});
            skLineSegment(sketch, "E28.6.19.0", {"start": v(-3.53, -10.42) * mm, "end": v(-3.39, -9.28) * mm});
            skLineSegment(sketch, "E28.1.20.0", {"start": v(-0.97, -9.83) * mm, "end": v(-1.34, -10.92) * mm});
            skLineSegment(sketch, "E28.3.20.0", {"start": v(-1.94, -10.83) * mm, "end": v(-1.34, -10.92) * mm});
            skLineSegment(sketch, "E28.6.20.0", {"start": v(-1.94, -10.83) * mm, "end": v(-1.97, -9.68) * mm});
            skLineSegment(sketch, "E28.1.21.0", {"start": v(0.5, -9.86) * mm, "end": v(0.3, -11) * mm});
            skLineSegment(sketch, "E28.3.21.0", {"start": v(-0.3, -11) * mm, "end": v(0.3, -11) * mm});
            skLineSegment(sketch, "E28.6.21.0", {"start": v(-0.3, -11) * mm, "end": v(-0.5, -9.86) * mm});
            skLineSegment(sketch, "E28.1.22.0", {"start": v(1.97, -9.68) * mm, "end": v(1.94, -10.83) * mm});
            skLineSegment(sketch, "E28.3.22.0", {"start": v(1.34, -10.92) * mm, "end": v(1.94, -10.83) * mm});
            skLineSegment(sketch, "E28.6.22.0", {"start": v(1.34, -10.92) * mm, "end": v(0.97, -9.83) * mm});
            skLineSegment(sketch, "E28.1.23.0", {"start": v(3.39, -9.28) * mm, "end": v(3.53, -10.42) * mm});
            skLineSegment(sketch, "E28.3.23.0", {"start": v(2.95, -10.6) * mm, "end": v(3.53, -10.42) * mm});
            skLineSegment(sketch, "E28.6.23.0", {"start": v(2.95, -10.6) * mm, "end": v(2.43, -9.57) * mm});
            skLineSegment(sketch, "E28.1.24.0", {"start": v(4.73, -8.67) * mm, "end": v(5.04, -9.78) * mm});
            skLineSegment(sketch, "E28.3.24.0", {"start": v(4.5, -10.04) * mm, "end": v(5.04, -9.78) * mm});
            skLineSegment(sketch, "E28.6.24.0", {"start": v(4.5, -10.04) * mm, "end": v(3.83, -9.1) * mm});
            skLineSegment(sketch, "E28.1.25.0", {"start": v(5.97, -7.87) * mm, "end": v(6.44, -8.91) * mm});
            skLineSegment(sketch, "E28.3.25.0", {"start": v(5.94, -9.26) * mm, "end": v(6.44, -8.91) * mm});
            skLineSegment(sketch, "E28.6.25.0", {"start": v(5.94, -9.26) * mm, "end": v(5.14, -8.43) * mm});
            skLineSegment(sketch, "E28.1.26.0", {"start": v(7.08, -6.89) * mm, "end": v(7.7, -7.85) * mm});
            skLineSegment(sketch, "E28.3.26.0", {"start": v(7.26, -8.27) * mm, "end": v(7.7, -7.85) * mm});
            skLineSegment(sketch, "E28.6.26.0", {"start": v(7.26, -8.27) * mm, "end": v(6.34, -7.57) * mm});
            skLineSegment(sketch, "E28.1.27.0", {"start": v(8.02, -5.76) * mm, "end": v(8.79, -6.62) * mm});
            skLineSegment(sketch, "E28.3.27.0", {"start": v(8.4, -7.1) * mm, "end": v(8.79, -6.62) * mm});
            skLineSegment(sketch, "E28.6.27.0", {"start": v(8.4, -7.1) * mm, "end": v(7.4, -6.54) * mm});
            skLineSegment(sketch, "E28.1.28.0", {"start": v(8.8, -4.5) * mm, "end": v(9.67, -5.24) * mm});
            skLineSegment(sketch, "E28.3.28.0", {"start": v(9.37, -5.76) * mm, "end": v(9.67, -5.24) * mm});
            skLineSegment(sketch, "E28.6.28.0", {"start": v(9.37, -5.76) * mm, "end": v(8.29, -5.37) * mm});
            skLineSegment(sketch, "E28.1.29.0", {"start": v(9.36, -3.14) * mm, "end": v(10.35, -3.74) * mm});
            skLineSegment(sketch, "E28.3.29.0", {"start": v(10.13, -4.3) * mm, "end": v(10.35, -3.74) * mm});
            skLineSegment(sketch, "E28.6.29.0", {"start": v(10.13, -4.3) * mm, "end": v(9, -4.07) * mm});
            skLineSegment(sketch, "E28.1.30.0", {"start": v(9.73, -1.7) * mm, "end": v(10.79, -2.15) * mm});
            skLineSegment(sketch, "E28.3.30.0", {"start": v(10.65, -2.74) * mm, "end": v(10.79, -2.15) * mm});
            skLineSegment(sketch, "E28.6.30.0", {"start": v(10.65, -2.74) * mm, "end": v(9.5, -2.68) * mm});
            skLineSegment(sketch, "E28.1.31.0", {"start": v(9.87, -0.24) * mm, "end": v(10.99, -0.52) * mm});
            skLineSegment(sketch, "E28.3.31.0", {"start": v(10.94, -1.12) * mm, "end": v(10.99, -0.52) * mm});
            skLineSegment(sketch, "E28.6.31.0", {"start": v(10.94, -1.12) * mm, "end": v(9.8, -1.24) * mm});
            skLineSegment(sketch, "E28.1.32.0", {"start": v(9.8, 1.24) * mm, "end": v(10.94, 1.12) * mm});
            skLineSegment(sketch, "E28.3.32.0", {"start": v(10.99, 0.52) * mm, "end": v(10.94, 1.12) * mm});
            skLineSegment(sketch, "E28.6.32.0", {"start": v(10.99, 0.52) * mm, "end": v(9.87, 0.24) * mm});
            skLineSegment(sketch, "E28.1.33.0", {"start": v(9.5, 2.68) * mm, "end": v(10.65, 2.74) * mm});
            skLineSegment(sketch, "E28.3.33.0", {"start": v(10.79, 2.15) * mm, "end": v(10.65, 2.74) * mm});
            skLineSegment(sketch, "E28.6.33.0", {"start": v(10.79, 2.15) * mm, "end": v(9.73, 1.7) * mm});
            skLineSegment(sketch, "E28.1.34.0", {"start": v(9, 4.07) * mm, "end": v(10.13, 4.3) * mm});
            skLineSegment(sketch, "E28.3.34.0", {"start": v(10.35, 3.74) * mm, "end": v(10.13, 4.3) * mm});
            skLineSegment(sketch, "E28.6.34.0", {"start": v(10.35, 3.74) * mm, "end": v(9.36, 3.14) * mm});
            skLineSegment(sketch, "E28.1.35.0", {"start": v(8.29, 5.37) * mm, "end": v(9.37, 5.76) * mm});
            skLineSegment(sketch, "E28.3.35.0", {"start": v(9.67, 5.24) * mm, "end": v(9.37, 5.76) * mm});
            skLineSegment(sketch, "E28.6.35.0", {"start": v(9.67, 5.24) * mm, "end": v(8.8, 4.5) * mm});
            skLineSegment(sketch, "E28.1.36.0", {"start": v(7.4, 6.54) * mm, "end": v(8.4, 7.1) * mm});
            skLineSegment(sketch, "E28.3.36.0", {"start": v(8.79, 6.62) * mm, "end": v(8.4, 7.1) * mm});
            skLineSegment(sketch, "E28.6.36.0", {"start": v(8.79, 6.62) * mm, "end": v(8.02, 5.76) * mm});
            skLineSegment(sketch, "E28.1.37.0", {"start": v(6.34, 7.57) * mm, "end": v(7.26, 8.27) * mm});
            skLineSegment(sketch, "E28.3.37.0", {"start": v(7.7, 7.85) * mm, "end": v(7.26, 8.27) * mm});
            skLineSegment(sketch, "E28.6.37.0", {"start": v(7.7, 7.85) * mm, "end": v(7.08, 6.89) * mm});
            skLineSegment(sketch, "E28.1.38.0", {"start": v(5.14, 8.43) * mm, "end": v(5.94, 9.26) * mm});
            skLineSegment(sketch, "E28.3.38.0", {"start": v(6.44, 8.91) * mm, "end": v(5.94, 9.26) * mm});
            skLineSegment(sketch, "E28.6.38.0", {"start": v(6.44, 8.91) * mm, "end": v(5.97, 7.87) * mm});
            skLineSegment(sketch, "E28.1.39.0", {"start": v(3.83, 9.1) * mm, "end": v(4.5, 10.04) * mm});
            skLineSegment(sketch, "E28.3.39.0", {"start": v(5.04, 9.78) * mm, "end": v(4.5, 10.04) * mm});
            skLineSegment(sketch, "E28.6.39.0", {"start": v(5.04, 9.78) * mm, "end": v(4.73, 8.67) * mm});
            skLineSegment(sketch, "E28.1.40.0", {"start": v(2.43, 9.57) * mm, "end": v(2.95, 10.6) * mm});
            skLineSegment(sketch, "E28.3.40.0", {"start": v(3.53, 10.42) * mm, "end": v(2.95, 10.6) * mm});
            skLineSegment(sketch, "E28.6.40.0", {"start": v(3.53, 10.42) * mm, "end": v(3.39, 9.28) * mm});
            skLineSegment(sketch, "E28.1.41.0", {"start": v(0.97, 9.83) * mm, "end": v(1.34, 10.92) * mm});
            skLineSegment(sketch, "E28.3.41.0", {"start": v(1.94, 10.83) * mm, "end": v(1.34, 10.92) * mm});
            skLineSegment(sketch, "E28.6.41.0", {"start": v(1.94, 10.83) * mm, "end": v(1.97, 9.68) * mm});
            skSolve(sketch);
        }
        {
            var Q0;
            Q0=qSketchRegion(id+"F2",true);
            extrude(context, id + "F3", {"entities" : qUnion([Q0]), "operationType" : NewBodyOperationType.ADD, "depth" : 4.5 * mm, "offsetDistance" : 25 * mm});
        }
        {
            var Q0;
            Q0=makeQuery(id+"F3.opExtrude","CAP_FACE",FACE,{"disambiguationData":[OSD([sQuery(id+"F2.wireOp",EDGE,"E18"),sQuery(id+"F2.wireOp",EDGE,"E23"),sQuery(id+"F2.wireOp",EDGE,"E24"),sQuery(id+"F2.wireOp",EDGE,"E25"),sQuery(id+"F2.wireOp",EDGE,"E26.1.0"),sQuery(id+"F2.wireOp",EDGE,"E26.1.1"),sQuery(id+"F2.wireOp",EDGE,"E26.1.2"),sQuery(id+"F2.wireOp",EDGE,"E26.2.0"),sQuery(id+"F2.wireOp",EDGE,"E26.2.1"),sQuery(id+"F2.wireOp",EDGE,"E26.2.2"),sQuery(id+"F2.wireOp",EDGE,"E27.1.3.0"),sQuery(id+"F2.wireOp",EDGE,"E27.3.3.0"),sQuery(id+"F2.wireOp",EDGE,"E27.6.3.0"),sQuery(id+"F2.wireOp",EDGE,"E27.1.4.0"),sQuery(id+"F2.wireOp",EDGE,"E27.3.4.0"),sQuery(id+"F2.wireOp",EDGE,"E27.6.4.0"),sQuery(id+"F2.wireOp",EDGE,"E27.1.5.0"),sQuery(id+"F2.wireOp",EDGE,"E27.3.5.0"),sQuery(id+"F2.wireOp",EDGE,"E27.6.5.0"),sQuery(id+"F2.wireOp",EDGE,"E27.1.6.0"),sQuery(id+"F2.wireOp",EDGE,"E27.3.6.0"),sQuery(id+"F2.wireOp",EDGE,"E27.6.6.0"),sQuery(id+"F2.wireOp",EDGE,"E27.1.7.0"),sQuery(id+"F2.wireOp",EDGE,"E27.3.7.0"),sQuery(id+"F2.wireOp",EDGE,"E27.6.7.0"),sQuery(id+"F2.wireOp",EDGE,"E27.1.8.0"),sQuery(id+"F2.wireOp",EDGE,"E27.3.8.0"),sQuery(id+"F2.wireOp",EDGE,"E27.6.8.0"),sQuery(id+"F2.wireOp",EDGE,"E27.1.9.0"),sQuery(id+"F2.wireOp",EDGE,"E27.3.9.0"),sQuery(id+"F2.wireOp",EDGE,"E27.6.9.0")])],"isStart":false});
            var sketch = newSketch(context, id + "F4", { "sketchPlane" : qUnion([Q0])});
            skCircle(sketch, "E29", {"center": v(0, 0) * mm, "radius": 1.05 * mm});
            skSolve(sketch);
        }
        {
            var Q0;
            Q0=qSketchRegion(id+"F4",true);
            extrude(context, id + "F5", {"entities" : qUnion([Q0]), "operationType" : NewBodyOperationType.REMOVE, "endBound" : BoundingType.THROUGH_ALL, "oppositeDirection" : true, "depth" : 25 * mm, "offsetDistance" : 25 * mm});
        }
        {
            var Q0;
            Q0=makeQuery(id+"F3.opExtrude","CAP_FACE",FACE,{"disambiguationData":[OSD([sQuery(id+"F2.wireOp",EDGE,"E18"),sQuery(id+"F2.wireOp",EDGE,"E23"),sQuery(id+"F2.wireOp",EDGE,"E24"),sQuery(id+"F2.wireOp",EDGE,"E25"),sQuery(id+"F2.wireOp",EDGE,"E26.1.0"),sQuery(id+"F2.wireOp",EDGE,"E26.1.1"),sQuery(id+"F2.wireOp",EDGE,"E26.1.2"),sQuery(id+"F2.wireOp",EDGE,"E26.2.0"),sQuery(id+"F2.wireOp",EDGE,"E26.2.1"),sQuery(id+"F2.wireOp",EDGE,"E26.2.2"),sQuery(id+"F2.wireOp",EDGE,"E27.1.3.0"),sQuery(id+"F2.wireOp",EDGE,"E27.3.3.0"),sQuery(id+"F2.wireOp",EDGE,"E27.6.3.0"),sQuery(id+"F2.wireOp",EDGE,"E27.1.4.0"),sQuery(id+"F2.wireOp",EDGE,"E27.3.4.0"),sQuery(id+"F2.wireOp",EDGE,"E27.6.4.0"),sQuery(id+"F2.wireOp",EDGE,"E27.1.5.0"),sQuery(id+"F2.wireOp",EDGE,"E27.3.5.0"),sQuery(id+"F2.wireOp",EDGE,"E27.6.5.0"),sQuery(id+"F2.wireOp",EDGE,"E27.1.6.0"),sQuery(id+"F2.wireOp",EDGE,"E27.3.6.0"),sQuery(id+"F2.wireOp",EDGE,"E27.6.6.0"),sQuery(id+"F2.wireOp",EDGE,"E27.1.7.0"),sQuery(id+"F2.wireOp",EDGE,"E27.3.7.0"),sQuery(id+"F2.wireOp",EDGE,"E27.6.7.0"),sQuery(id+"F2.wireOp",EDGE,"E27.1.8.0"),sQuery(id+"F2.wireOp",EDGE,"E27.3.8.0"),sQuery(id+"F2.wireOp",EDGE,"E27.6.8.0"),sQuery(id+"F2.wireOp",EDGE,"E27.1.9.0"),sQuery(id+"F2.wireOp",EDGE,"E27.3.9.0"),sQuery(id+"F2.wireOp",EDGE,"E27.6.9.0"),sQuery(id+"F2.wireOp",EDGE,"E28.1.10.0"),sQuery(id+"F2.wireOp",EDGE,"E28.3.10.0"),sQuery(id+"F2.wireOp",EDGE,"E28.6.10.0"),sQuery(id+"F2.wireOp",EDGE,"E28.1.11.0"),sQuery(id+"F2.wireOp",EDGE,"E28.3.11.0"),sQuery(id+"F2.wireOp",EDGE,"E28.6.11.0"),sQuery(id+"F2.wireOp",EDGE,"E28.1.12.0"),sQuery(id+"F2.wireOp",EDGE,"E28.3.12.0"),sQuery(id+"F2.wireOp",EDGE,"E28.6.12.0"),sQuery(id+"F2.wireOp",EDGE,"E28.1.13.0"),sQuery(id+"F2.wireOp",EDGE,"E28.3.13.0"),sQuery(id+"F2.wireOp",EDGE,"E28.6.13.0"),sQuery(id+"F2.wireOp",EDGE,"E28.1.14.0"),sQuery(id+"F2.wireOp",EDGE,"E28.3.14.0"),sQuery(id+"F2.wireOp",EDGE,"E28.6.14.0"),sQuery(id+"F2.wireOp",EDGE,"E28.1.15.0"),sQuery(id+"F2.wireOp",EDGE,"E28.3.15.0"),sQuery(id+"F2.wireOp",EDGE,"E28.6.15.0"),sQuery(id+"F2.wireOp",EDGE,"E28.1.16.0"),sQuery(id+"F2.wireOp",EDGE,"E28.3.16.0"),sQuery(id+"F2.wireOp",EDGE,"E28.6.16.0"),sQuery(id+"F2.wireOp",EDGE,"E28.1.17.0"),sQuery(id+"F2.wireOp",EDGE,"E28.3.17.0"),sQuery(id+"F2.wireOp",EDGE,"E28.6.17.0"),sQuery(id+"F2.wireOp",EDGE,"E28.1.18.0"),sQuery(id+"F2.wireOp",EDGE,"E28.3.18.0"),sQuery(id+"F2.wireOp",EDGE,"E28.6.18.0"),sQuery(id+"F2.wireOp",EDGE,"E28.1.19.0"),sQuery(id+"F2.wireOp",EDGE,"E28.3.19.0"),sQuery(id+"F2.wireOp",EDGE,"E28.6.19.0"),sQuery(id+"F2.wireOp",EDGE,"E28.1.20.0"),sQuery(id+"F2.wireOp",EDGE,"E28.3.20.0"),sQuery(id+"F2.wireOp",EDGE,"E28.6.20.0"),sQuery(id+"F2.wireOp",EDGE,"E28.1.21.0"),sQuery(id+"F2.wireOp",EDGE,"E28.3.21.0"),sQuery(id+"F2.wireOp",EDGE,"E28.6.21.0"),sQuery(id+"F2.wireOp",EDGE,"E28.1.22.0"),sQuery(id+"F2.wireOp",EDGE,"E28.3.22.0"),sQuery(id+"F2.wireOp",EDGE,"E28.6.22.0"),sQuery(id+"F2.wireOp",EDGE,"E28.1.23.0"),sQuery(id+"F2.wireOp",EDGE,"E28.3.23.0"),sQuery(id+"F2.wireOp",EDGE,"E28.6.23.0"),sQuery(id+"F2.wireOp",EDGE,"E28.1.24.0"),sQuery(id+"F2.wireOp",EDGE,"E28.3.24.0"),sQuery(id+"F2.wireOp",EDGE,"E28.6.24.0"),sQuery(id+"F2.wireOp",EDGE,"E28.1.25.0"),sQuery(id+"F2.wireOp",EDGE,"E28.3.25.0"),sQuery(id+"F2.wireOp",EDGE,"E28.6.25.0"),sQuery(id+"F2.wireOp",EDGE,"E28.1.26.0"),sQuery(id+"F2.wireOp",EDGE,"E28.3.26.0"),sQuery(id+"F2.wireOp",EDGE,"E28.6.26.0"),sQuery(id+"F2.wireOp",EDGE,"E28.1.27.0"),sQuery(id+"F2.wireOp",EDGE,"E28.3.27.0"),sQuery(id+"F2.wireOp",EDGE,"E28.6.27.0"),sQuery(id+"F2.wireOp",EDGE,"E28.1.28.0"),sQuery(id+"F2.wireOp",EDGE,"E28.3.28.0"),sQuery(id+"F2.wireOp",EDGE,"E28.6.28.0"),sQuery(id+"F2.wireOp",EDGE,"E28.1.29.0"),sQuery(id+"F2.wireOp",EDGE,"E28.3.29.0"),sQuery(id+"F2.wireOp",EDGE,"E28.6.29.0"),sQuery(id+"F2.wireOp",EDGE,"E28.1.30.0"),sQuery(id+"F2.wireOp",EDGE,"E28.3.30.0"),sQuery(id+"F2.wireOp",EDGE,"E28.6.30.0"),sQuery(id+"F2.wireOp",EDGE,"E28.1.31.0"),sQuery(id+"F2.wireOp",EDGE,"E28.3.31.0"),sQuery(id+"F2.wireOp",EDGE,"E28.6.31.0"),sQuery(id+"F2.wireOp",EDGE,"E28.1.32.0"),sQuery(id+"F2.wireOp",EDGE,"E28.3.32.0"),sQuery(id+"F2.wireOp",EDGE,"E28.6.32.0"),sQuery(id+"F2.wireOp",EDGE,"E28.1.33.0"),sQuery(id+"F2.wireOp",EDGE,"E28.3.33.0"),sQuery(id+"F2.wireOp",EDGE,"E28.6.33.0"),sQuery(id+"F2.wireOp",EDGE,"E28.1.34.0"),sQuery(id+"F2.wireOp",EDGE,"E28.3.34.0"),sQuery(id+"F2.wireOp",EDGE,"E28.6.34.0"),sQuery(id+"F2.wireOp",EDGE,"E28.1.35.0"),sQuery(id+"F2.wireOp",EDGE,"E28.3.35.0"),sQuery(id+"F2.wireOp",EDGE,"E28.6.35.0"),sQuery(id+"F2.wireOp",EDGE,"E28.1.36.0"),sQuery(id+"F2.wireOp",EDGE,"E28.3.36.0"),sQuery(id+"F2.wireOp",EDGE,"E28.6.36.0"),sQuery(id+"F2.wireOp",EDGE,"E28.1.37.0"),sQuery(id+"F2.wireOp",EDGE,"E28.3.37.0"),sQuery(id+"F2.wireOp",EDGE,"E28.6.37.0"),sQuery(id+"F2.wireOp",EDGE,"E28.1.38.0"),sQuery(id+"F2.wireOp",EDGE,"E28.3.38.0"),sQuery(id+"F2.wireOp",EDGE,"E28.6.38.0"),sQuery(id+"F2.wireOp",EDGE,"E28.1.39.0"),sQuery(id+"F2.wireOp",EDGE,"E28.3.39.0"),sQuery(id+"F2.wireOp",EDGE,"E28.6.39.0"),sQuery(id+"F2.wireOp",EDGE,"E28.1.40.0"),sQuery(id+"F2.wireOp",EDGE,"E28.3.40.0"),sQuery(id+"F2.wireOp",EDGE,"E28.6.40.0"),sQuery(id+"F2.wireOp",EDGE,"E28.1.41.0"),sQuery(id+"F2.wireOp",EDGE,"E28.3.41.0"),sQuery(id+"F2.wireOp",EDGE,"E28.6.41.0")])],"isStart":false});
            var sketch = newSketch(context, id + "F6", { "sketchPlane" : qUnion([Q0])});
            skArc(sketch, "E30", {"start": v(0.74, -9.85) * mm, "mid": v(-8.55, 4.94) * mm, "end": v(8.9, 4.28) * mm});
            skArc(sketch, "E31", {"start": v(0.87, -11.7) * mm, "mid": v(-10.1, 5.98) * mm, "end": v(10.68, 4.85) * mm});
            skLineSegment(sketch, "E32", {"start": v(10.68, 4.85) * mm, "end": v(8.9, 4.28) * mm});
            skLineSegment(sketch, "E33", {"start": v(0.87, -11.7) * mm, "end": v(0.74, -9.85) * mm});
            skSolve(sketch);
        }
        {
            var Q0;
            Q0 = qSketchRegion(id + "F6", true);
            var Q1;
            Q1=makeQuery(id+"F1.opExtrude","CAP_FACE",FACE,{"disambiguationData":[OSD([sQuery(id+"F0.wireOp",EDGE,"E2"),sQuery(id+"F0.wireOp",EDGE,"E7"),sQuery(id+"F0.wireOp",EDGE,"E8"),sQuery(id+"F0.wireOp",EDGE,"E9"),sQuery(id+"F0.wireOp",EDGE,"E10.1.0"),sQuery(id+"F0.wireOp",EDGE,"E10.1.1"),sQuery(id+"F0.wireOp",EDGE,"E10.1.2"),sQuery(id+"F0.wireOp",EDGE,"E10.2.0"),sQuery(id+"F0.wireOp",EDGE,"E10.2.1"),sQuery(id+"F0.wireOp",EDGE,"E10.2.2"),sQuery(id+"F0.wireOp",EDGE,"E11.1.3.0"),sQuery(id+"F0.wireOp",EDGE,"E11.3.3.0"),sQuery(id+"F0.wireOp",EDGE,"E11.6.3.0"),sQuery(id+"F0.wireOp",EDGE,"E11.1.4.0"),sQuery(id+"F0.wireOp",EDGE,"E11.3.4.0"),sQuery(id+"F0.wireOp",EDGE,"E11.6.4.0"),sQuery(id+"F0.wireOp",EDGE,"E11.1.5.0"),sQuery(id+"F0.wireOp",EDGE,"E11.3.5.0"),sQuery(id+"F0.wireOp",EDGE,"E11.6.5.0"),sQuery(id+"F0.wireOp",EDGE,"E11.1.6.0"),sQuery(id+"F0.wireOp",EDGE,"E11.3.6.0"),sQuery(id+"F0.wireOp",EDGE,"E11.6.6.0"),sQuery(id+"F0.wireOp",EDGE,"E11.1.7.0"),sQuery(id+"F0.wireOp",EDGE,"E11.3.7.0"),sQuery(id+"F0.wireOp",EDGE,"E11.6.7.0"),sQuery(id+"F0.wireOp",EDGE,"E11.1.8.0"),sQuery(id+"F0.wireOp",EDGE,"E11.3.8.0"),sQuery(id+"F0.wireOp",EDGE,"E11.6.8.0"),sQuery(id+"F0.wireOp",EDGE,"E11.1.9.0"),sQuery(id+"F0.wireOp",EDGE,"E11.3.9.0"),sQuery(id+"F0.wireOp",EDGE,"E11.6.9.0"),sQuery(id+"F0.wireOp",EDGE,"E11.1.10.0"),sQuery(id+"F0.wireOp",EDGE,"E11.3.10.0"),sQuery(id+"F0.wireOp",EDGE,"E11.6.10.0"),sQuery(id+"F0.wireOp",EDGE,"E11.1.11.0"),sQuery(id+"F0.wireOp",EDGE,"E11.3.11.0"),sQuery(id+"F0.wireOp",EDGE,"E11.6.11.0"),sQuery(id+"F0.wireOp",EDGE,"E11.1.12.0"),sQuery(id+"F0.wireOp",EDGE,"E11.3.12.0"),sQuery(id+"F0.wireOp",EDGE,"E11.6.12.0"),sQuery(id+"F0.wireOp",EDGE,"E11.1.13.0"),sQuery(id+"F0.wireOp",EDGE,"E11.3.13.0"),sQuery(id+"F0.wireOp",EDGE,"E11.6.13.0"),sQuery(id+"F0.wireOp",EDGE,"E11.1.14.0"),sQuery(id+"F0.wireOp",EDGE,"E11.3.14.0"),sQuery(id+"F0.wireOp",EDGE,"E11.6.14.0"),sQuery(id+"F0.wireOp",EDGE,"E11.1.15.0"),sQuery(id+"F0.wireOp",EDGE,"E11.3.15.0"),sQuery(id+"F0.wireOp",EDGE,"E11.6.15.0"),sQuery(id+"F0.wireOp",EDGE,"E11.1.16.0"),sQuery(id+"F0.wireOp",EDGE,"E11.3.16.0"),sQuery(id+"F0.wireOp",EDGE,"E11.6.16.0"),sQuery(id+"F0.wireOp",EDGE,"E11.1.17.0"),sQuery(id+"F0.wireOp",EDGE,"E11.3.17.0"),sQuery(id+"F0.wireOp",EDGE,"E11.6.17.0"),sQuery(id+"F0.wireOp",EDGE,"E11.1.18.0"),sQuery(id+"F0.wireOp",EDGE,"E11.3.18.0"),sQuery(id+"F0.wireOp",EDGE,"E11.6.18.0"),sQuery(id+"F0.wireOp",EDGE,"E11.1.19.0"),sQuery(id+"F0.wireOp",EDGE,"E11.3.19.0"),sQuery(id+"F0.wireOp",EDGE,"E11.6.19.0"),sQuery(id+"F0.wireOp",EDGE,"E11.1.20.0"),sQuery(id+"F0.wireOp",EDGE,"E11.3.20.0"),sQuery(id+"F0.wireOp",EDGE,"E11.6.20.0"),sQuery(id+"F0.wireOp",EDGE,"E11.1.21.0"),sQuery(id+"F0.wireOp",EDGE,"E11.3.21.0"),sQuery(id+"F0.wireOp",EDGE,"E11.6.21.0"),sQuery(id+"F0.wireOp",EDGE,"E11.1.22.0"),sQuery(id+"F0.wireOp",EDGE,"E11.3.22.0"),sQuery(id+"F0.wireOp",EDGE,"E11.6.22.0"),sQuery(id+"F0.wireOp",EDGE,"E11.1.23.0"),sQuery(id+"F0.wireOp",EDGE,"E11.3.23.0"),sQuery(id+"F0.wireOp",EDGE,"E11.6.23.0"),sQuery(id+"F0.wireOp",EDGE,"E11.1.24.0"),sQuery(id+"F0.wireOp",EDGE,"E11.3.24.0"),sQuery(id+"F0.wireOp",EDGE,"E11.6.24.0"),sQuery(id+"F0.wireOp",EDGE,"E11.1.25.0"),sQuery(id+"F0.wireOp",EDGE,"E11.3.25.0"),sQuery(id+"F0.wireOp",EDGE,"E11.6.25.0"),sQuery(id+"F0.wireOp",EDGE,"E11.1.26.0"),sQuery(id+"F0.wireOp",EDGE,"E11.3.26.0"),sQuery(id+"F0.wireOp",EDGE,"E11.6.26.0"),sQuery(id+"F0.wireOp",EDGE,"E11.1.27.0"),sQuery(id+"F0.wireOp",EDGE,"E11.3.27.0"),sQuery(id+"F0.wireOp",EDGE,"E11.6.27.0"),sQuery(id+"F0.wireOp",EDGE,"E11.1.28.0"),sQuery(id+"F0.wireOp",EDGE,"E11.3.28.0"),sQuery(id+"F0.wireOp",EDGE,"E11.6.28.0"),sQuery(id+"F0.wireOp",EDGE,"E11.1.29.0"),sQuery(id+"F0.wireOp",EDGE,"E11.3.29.0"),sQuery(id+"F0.wireOp",EDGE,"E11.6.29.0"),sQuery(id+"F0.wireOp",EDGE,"E12.1.30.0"),sQuery(id+"F0.wireOp",EDGE,"E12.3.30.0"),sQuery(id+"F0.wireOp",EDGE,"E12.6.30.0"),sQuery(id+"F0.wireOp",EDGE,"E12.1.31.0"),sQuery(id+"F0.wireOp",EDGE,"E12.3.31.0"),sQuery(id+"F0.wireOp",EDGE,"E12.6.31.0"),sQuery(id+"F0.wireOp",EDGE,"E12.1.32.0"),sQuery(id+"F0.wireOp",EDGE,"E12.3.32.0"),sQuery(id+"F0.wireOp",EDGE,"E12.6.32.0"),sQuery(id+"F0.wireOp",EDGE,"E12.1.33.0"),sQuery(id+"F0.wireOp",EDGE,"E12.3.33.0"),sQuery(id+"F0.wireOp",EDGE,"E12.6.33.0"),sQuery(id+"F0.wireOp",EDGE,"E12.1.34.0"),sQuery(id+"F0.wireOp",EDGE,"E12.3.34.0"),sQuery(id+"F0.wireOp",EDGE,"E12.6.34.0"),sQuery(id+"F0.wireOp",EDGE,"E12.1.35.0"),sQuery(id+"F0.wireOp",EDGE,"E12.3.35.0"),sQuery(id+"F0.wireOp",EDGE,"E12.6.35.0"),sQuery(id+"F0.wireOp",EDGE,"E12.1.36.0"),sQuery(id+"F0.wireOp",EDGE,"E12.3.36.0"),sQuery(id+"F0.wireOp",EDGE,"E12.6.36.0"),sQuery(id+"F0.wireOp",EDGE,"E12.1.37.0"),sQuery(id+"F0.wireOp",EDGE,"E12.3.37.0"),sQuery(id+"F0.wireOp",EDGE,"E12.6.37.0"),sQuery(id+"F0.wireOp",EDGE,"E12.1.38.0"),sQuery(id+"F0.wireOp",EDGE,"E12.3.38.0"),sQuery(id+"F0.wireOp",EDGE,"E12.6.38.0"),sQuery(id+"F0.wireOp",EDGE,"E12.1.39.0"),sQuery(id+"F0.wireOp",EDGE,"E12.3.39.0"),sQuery(id+"F0.wireOp",EDGE,"E12.6.39.0"),sQuery(id+"F0.wireOp",EDGE,"E12.1.40.0"),sQuery(id+"F0.wireOp",EDGE,"E12.3.40.0"),sQuery(id+"F0.wireOp",EDGE,"E12.6.40.0"),sQuery(id+"F0.wireOp",EDGE,"E12.1.41.0"),sQuery(id+"F0.wireOp",EDGE,"E12.3.41.0"),sQuery(id+"F0.wireOp",EDGE,"E12.6.41.0"),sQuery(id+"F0.wireOp",EDGE,"E13.1.42.0"),sQuery(id+"F0.wireOp",EDGE,"E13.3.42.0"),sQuery(id+"F0.wireOp",EDGE,"E13.6.42.0"),sQuery(id+"F0.wireOp",EDGE,"E13.1.43.0"),sQuery(id+"F0.wireOp",EDGE,"E13.3.43.0"),sQuery(id+"F0.wireOp",EDGE,"E13.6.43.0"),sQuery(id+"F0.wireOp",EDGE,"E13.1.44.0"),sQuery(id+"F0.wireOp",EDGE,"E13.3.44.0"),sQuery(id+"F0.wireOp",EDGE,"E13.6.44.0"),sQuery(id+"F0.wireOp",EDGE,"E13.1.45.0"),sQuery(id+"F0.wireOp",EDGE,"E13.3.45.0"),sQuery(id+"F0.wireOp",EDGE,"E13.6.45.0"),sQuery(id+"F0.wireOp",EDGE,"E13.1.46.0"),sQuery(id+"F0.wireOp",EDGE,"E13.3.46.0"),sQuery(id+"F0.wireOp",EDGE,"E13.6.46.0"),sQuery(id+"F0.wireOp",EDGE,"E13.1.47.0"),sQuery(id+"F0.wireOp",EDGE,"E13.3.47.0"),sQuery(id+"F0.wireOp",EDGE,"E13.6.47.0"),sQuery(id+"F0.wireOp",EDGE,"E14.1.48.0"),sQuery(id+"F0.wireOp",EDGE,"E14.3.48.0"),sQuery(id+"F0.wireOp",EDGE,"E14.6.48.0"),sQuery(id+"F0.wireOp",EDGE,"E14.1.49.0"),sQuery(id+"F0.wireOp",EDGE,"E14.3.49.0"),sQuery(id+"F0.wireOp",EDGE,"E14.6.49.0"),sQuery(id+"F0.wireOp",EDGE,"E14.1.50.0"),sQuery(id+"F0.wireOp",EDGE,"E14.3.50.0"),sQuery(id+"F0.wireOp",EDGE,"E14.6.50.0"),sQuery(id+"F0.wireOp",EDGE,"E14.1.51.0"),sQuery(id+"F0.wireOp",EDGE,"E14.3.51.0"),sQuery(id+"F0.wireOp",EDGE,"E14.6.51.0"),sQuery(id+"F0.wireOp",EDGE,"E14.1.52.0"),sQuery(id+"F0.wireOp",EDGE,"E14.3.52.0"),sQuery(id+"F0.wireOp",EDGE,"E14.6.52.0"),sQuery(id+"F0.wireOp",EDGE,"E14.1.53.0"),sQuery(id+"F0.wireOp",EDGE,"E14.3.53.0"),sQuery(id+"F0.wireOp",EDGE,"E14.6.53.0"),sQuery(id+"F0.wireOp",EDGE,"E15.1.54.0"),sQuery(id+"F0.wireOp",EDGE,"E15.3.54.0"),sQuery(id+"F0.wireOp",EDGE,"E15.6.54.0"),sQuery(id+"F0.wireOp",EDGE,"E15.1.55.0"),sQuery(id+"F0.wireOp",EDGE,"E15.3.55.0"),sQuery(id+"F0.wireOp",EDGE,"E15.6.55.0"),sQuery(id+"F0.wireOp",EDGE,"E15.1.56.0"),sQuery(id+"F0.wireOp",EDGE,"E15.3.56.0"),sQuery(id+"F0.wireOp",EDGE,"E15.6.56.0"),sQuery(id+"F0.wireOp",EDGE,"E15.1.57.0"),sQuery(id+"F0.wireOp",EDGE,"E15.3.57.0"),sQuery(id+"F0.wireOp",EDGE,"E15.6.57.0"),sQuery(id+"F0.wireOp",EDGE,"E15.1.58.0"),sQuery(id+"F0.wireOp",EDGE,"E15.3.58.0"),sQuery(id+"F0.wireOp",EDGE,"E15.6.58.0"),sQuery(id+"F0.wireOp",EDGE,"E15.1.59.0"),sQuery(id+"F0.wireOp",EDGE,"E15.3.59.0"),sQuery(id+"F0.wireOp",EDGE,"E15.6.59.0")])],"isStart":false});
            extrude(context, id + "F7", {"entities" : qUnion([Q0]), "operationType" : NewBodyOperationType.REMOVE, "endBound" : BoundingType.UP_TO_SURFACE, "oppositeDirection" : true, "depth" : 25 * mm, "endBoundEntityFace" : qUnion([Q1]), "offsetDistance" : 25 * mm});
        }
    });
